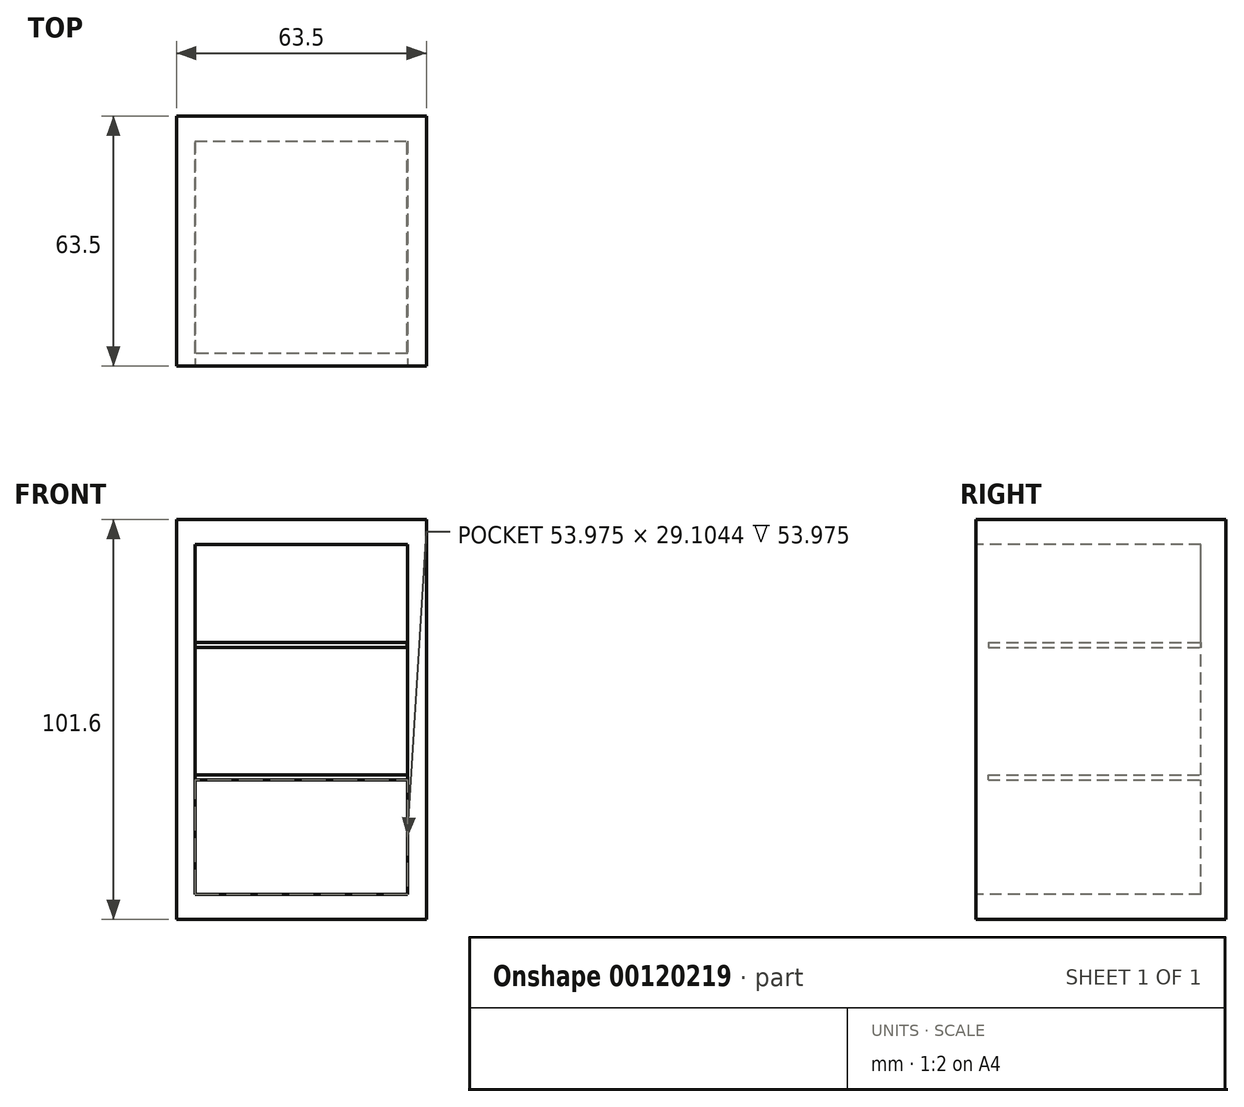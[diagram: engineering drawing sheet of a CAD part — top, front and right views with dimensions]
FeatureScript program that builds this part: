
annotation { "Feature Type Name" : "Feature", "Feature Type Description" : "" }
export const myFeature = defineFeature(function(context is Context, id is Id, definition is map)
    precondition{}
    {
        {
            var Q0;
            Q0=qCreatedBy(makeId("Front.planeOp"),FACE);
            var sketch = newSketch(context, id + "F0", { "sketchPlane" : qUnion([Q0])});
            skLineSegment(sketch, "E0.bottom", {"start": v(31.75, -50.8) * mm, "end": v(-31.75, -50.8) * mm});
            skLineSegment(sketch, "E0.top", {"start": v(31.75, 50.8) * mm, "end": v(-31.75, 50.8) * mm});
            skLineSegment(sketch, "E0.left", {"start": v(31.75, -50.8) * mm, "end": v(31.75, 50.8) * mm});
            skLineSegment(sketch, "E0.right", {"start": v(-31.75, -50.8) * mm, "end": v(-31.75, 50.8) * mm});
            skPoint(sketch, "E0.middle", {"position": v(0, 0) * mm});
            skSolve(sketch);
        }
        {
            var Q0;
            Q0=makeQuery(id+"F0.imprint","IMPRINT",FACE,{"disambiguationData":[TD([[makeQuery(id+"F0.imprint","IMPRINT",EDGE,{"derivedFrom":sQuery(id+"F0.wireOp",EDGE,"E0.bottom")}),-1.0]])]});
            extrude(context, id + "F1", {"entities" : qUnion([Q0]), "endBound" : BoundingType.SYMMETRIC, "depth" : 63.5 * mm});
        }
        {
            var Q0;
            Q0=makeQuery(id+"F1.opExtrude","CAP_FACE",FACE,{"disambiguationData":[OSD([sQuery(id+"F0.wireOp",EDGE,"E0.bottom"),sQuery(id+"F0.wireOp",EDGE,"E0.top"),sQuery(id+"F0.wireOp",EDGE,"E0.left"),sQuery(id+"F0.wireOp",EDGE,"E0.right")])],"isStart":false});
            var sketch = newSketch(context, id + "F2", { "sketchPlane" : qUnion([Q0])});
            skLineSegment(sketch, "E1.bottom", {"start": v(26.99, -44.45) * mm, "end": v(-26.99, -44.45) * mm});
            skLineSegment(sketch, "E1.top", {"start": v(26.99, 44.45) * mm, "end": v(-26.99, 44.45) * mm});
            skLineSegment(sketch, "E1.left", {"start": v(26.99, -44.45) * mm, "end": v(26.99, 44.45) * mm});
            skLineSegment(sketch, "E1.right", {"start": v(-26.99, -44.45) * mm, "end": v(-26.99, 44.45) * mm});
            skPoint(sketch, "E1.middle", {"position": v(0, 0) * mm});
            skSolve(sketch);
        }
        {
            var Q0;
            Q0=makeQuery(id+"F2.imprint","IMPRINT",FACE,{"disambiguationData":[TD([[makeQuery(id+"F2.imprint","IMPRINT",EDGE,{"derivedFrom":sQuery(id+"F2.wireOp",EDGE,"E1.bottom")}),-1.0]])]});
            extrude(context, id + "F3", {"entities" : qUnion([Q0]), "operationType" : NewBodyOperationType.REMOVE, "oppositeDirection" : true, "depth" : 57.15 * mm});
        }
        {
            var Q0;
            Q0=qCreatedBy(makeId("Front.planeOp"),FACE);
            var sketch = newSketch(context, id + "F4", { "sketchPlane" : qUnion([Q0])});
            skLineSegment(sketch, "E2.bottom", {"start": v(26.99, -15.35) * mm, "end": v(-26.99, -15.35) * mm});
            skLineSegment(sketch, "E2.top", {"start": v(26.99, -14.08) * mm, "end": v(-26.99, -14.08) * mm});
            skLineSegment(sketch, "E2.left", {"start": v(26.99, -15.35) * mm, "end": v(26.99, -14.08) * mm});
            skLineSegment(sketch, "E2.right", {"start": v(-26.99, -15.35) * mm, "end": v(-26.99, -14.08) * mm});
            skPoint(sketch, "E2.middle", {"position": v(0, -14.71) * mm});
            skLineSegment(sketch, "E3.bottom", {"start": v(26.9, 18.36) * mm, "end": v(-27.08, 18.36) * mm});
            skLineSegment(sketch, "E3.top", {"start": v(26.9, 19.63) * mm, "end": v(-27.08, 19.63) * mm});
            skLineSegment(sketch, "E3.left", {"start": v(26.9, 18.36) * mm, "end": v(26.9, 19.63) * mm});
            skLineSegment(sketch, "E3.right", {"start": v(-27.08, 18.36) * mm, "end": v(-27.08, 19.63) * mm});
            skPoint(sketch, "E3.middle", {"position": v(-0.09, 19) * mm});
            skSolve(sketch);
        }
        {
            var Q0;
            Q0=makeQuery(id+"F4.imprint","IMPRINT",FACE,{"disambiguationData":[TD([[makeQuery(id+"F4.imprint","IMPRINT",EDGE,{"derivedFrom":sQuery(id+"F4.wireOp",EDGE,"E3.bottom")}),-1.0]])]});
            var Q1;
            Q1=makeQuery(id+"F4.imprint","IMPRINT",FACE,{"disambiguationData":[TD([[makeQuery(id+"F4.imprint","IMPRINT",EDGE,{"derivedFrom":sQuery(id+"F4.wireOp",EDGE,"E2.bottom")}),-1.0]])]});
            extrude(context, id + "F5", {"entities" : qUnion([Q0, Q1]), "operationType" : NewBodyOperationType.ADD, "endBound" : BoundingType.SYMMETRIC, "depth" : 57.15 * mm});
        }
    });
